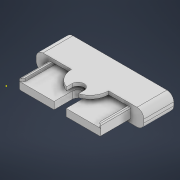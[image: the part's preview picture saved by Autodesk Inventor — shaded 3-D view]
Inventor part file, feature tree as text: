
AUTODESK INVENTOR PART (.ipt)
format: ipt  version: 2022 (Build 260153000, 153)  size: 476,672 bytes
history: native  units: mm
features: sketch x13, extrude x10, fillet x3, emboss x1
ambient origin geometry x8: Origin, YZ Plane, XZ Plane, XY Plane, X Axis, Y Axis, Z Axis, Center Point
bodies: Body1 (feature_tree)
feature tree (27):
  extrude  "Extrusion8"  Depth=10.0mm
  extrude  "Extrusion9"  Depth=10.5mm
  extrude  "Extrusion10"  Depth=7.0mm TaperAngle=0.0deg
  extrude  "Extrusion11"  Depth=17.5mm
  extrude  "Extrusion12"  Depth=2.0mm TaperAngle=0.0deg
  fillet  "Fillet5"  Radius=33.0mm
  extrude  "Extrusion13"  Depth=17.5mm
  fillet  "Fillet6"  Radius=17.5mm
  emboss  "Emboss3"
  sketch  "Sketch22"  dims[d64=0.2mm d65=0.0mm d66=0.2mm d67=0.0mm d68=1.8mm]
  extrude  "Extrusion14"  Depth=1.0mm TaperAngle=0.0deg
  extrude  "Extrusion15"  Depth=1.8mm TaperAngle=0.0deg
  fillet  "Fillet7"  Radius=1.8mm
  sketch  "Sketch25"  dims[d83=30.0mm d84=0.0mm]
  extrude  "Extrusion18"  Depth=4.0mm
  extrude  "Extrusion19"  Depth=17.5mm TaperAngle=0.0deg
  sketch  "Sketch13"  dims[d38=63.0mm d39=10.0mm]
  sketch  "Sketch15"  dims[d40=35.0mm d41=0.0mm d42=10.5mm]
  sketch  "Sketch16"  dims[d43=7.0mm d44=35.0mm d45=0.0mm]
  sketch  "Sketch17"  dims[d46=63.0mm d47=17.5mm]
  sketch  "Sketch19"  dims[d48=2.0mm d49=0.0mm d51=2.0mm d52=0.0mm d55=33.0mm d56=0.0mm]
  sketch  "Sketch20"  dims[d57=2.0mm d58=48.0mm d59=17.5mm d60=0.0mm]
  sketch  "Sketch21"  dims[d61=1.0mm d62=1.0mm d63=0.0mm]
  sketch  "Sketch23"  dims[d69=4.0mm d71=63.0mm]
  sketch  "Sketch24"  dims[d72=17.5mm d81=3.8mm d82=0.0mm]
  sketch  "Sketch28"  dims[d89=21.7mm]
  sketch  "Sketch29"  dims[d87=0.5mm d88=0.872665mm d90=0.872665mm]
